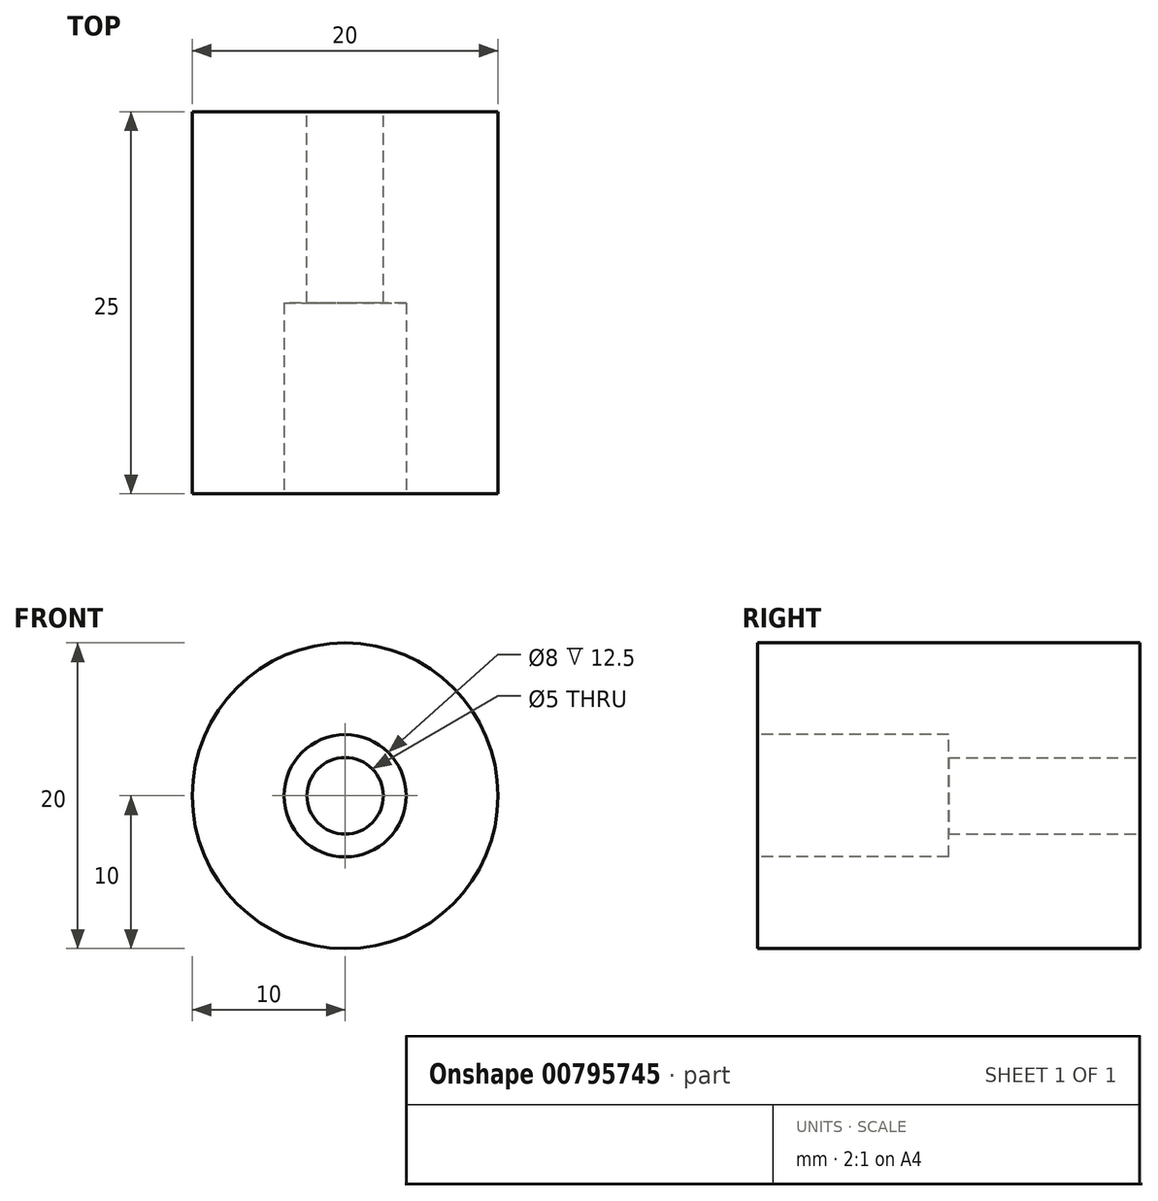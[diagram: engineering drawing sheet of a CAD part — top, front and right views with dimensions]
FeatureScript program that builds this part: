
annotation { "Feature Type Name" : "Feature", "Feature Type Description" : "" }
export const myFeature = defineFeature(function(context is Context, id is Id, definition is map)
    precondition{}
    {
        {
            var Q0;
            Q0=qCreatedBy(makeId("Front.planeOp"),FACE);
            var sketch = newSketch(context, id + "F0", { "sketchPlane" : qUnion([Q0])});
            skCircle(sketch, "E0", {"center": v(0, 0) * mm, "radius": 10 * mm});
            skSolve(sketch);
        }
        {
            var Q0;
            Q0=makeQuery(id+"F0.imprint","IMPRINT",FACE,{"disambiguationData":[TD([[makeQuery(id+"F0.imprint","IMPRINT",EDGE,{"derivedFrom":sQuery(id+"F0.wireOp",EDGE,"E0")}),1.0]])]});
            extrude(context, id + "F1", {"entities" : qUnion([Q0]), "depth" : 25 * mm, "offsetDistance" : 25 * mm});
        }
        {
            var Q0;
            Q0=makeQuery(id+"F1.opExtrude","CAP_FACE",FACE,{"disambiguationData":[OSD([sQuery(id+"F0.wireOp",EDGE,"E0")])],"isStart":false});
            var sketch = newSketch(context, id + "F2", { "sketchPlane" : qUnion([Q0])});
            skCircle(sketch, "E1", {"center": v(0, 0) * mm, "radius": 4 * mm});
            skSolve(sketch);
        }
        {
            var Q0;
            Q0=makeQuery(id+"F2.imprint","IMPRINT",FACE,{"disambiguationData":[TD([[makeQuery(id+"F2.imprint","IMPRINT",EDGE,{"derivedFrom":sQuery(id+"F2.wireOp",EDGE,"E1")}),1.0]])]});
            extrude(context, id + "F3", {"entities" : qUnion([Q0]), "operationType" : NewBodyOperationType.REMOVE, "oppositeDirection" : true, "depth" : 12.5 * mm, "offsetDistance" : 25 * mm});
        }
        {
            var Q0;
            Q0=makeQuery(id+"F1.opExtrude","CAP_FACE",FACE,{"disambiguationData":[OSD([sQuery(id+"F0.wireOp",EDGE,"E0")])],"isStart":true});
            var sketch = newSketch(context, id + "F4", { "sketchPlane" : qUnion([Q0])});
            skCircle(sketch, "E2", {"center": v(0, 0) * mm, "radius": 2.5 * mm});
            skSolve(sketch);
        }
        {
            var Q0;
            Q0 = qSketchRegion(id + "F4", true);
            extrude(context, id + "F5", {"entities" : qUnion([Q0]), "operationType" : NewBodyOperationType.REMOVE, "oppositeDirection" : true, "depth" : 12.5 * mm, "offsetDistance" : 25 * mm});
        }
    });
